# Revit family: P6 UNO XL steel base 100x100
name_source: partatom
category: Furniture
revit_build: Autodesk Revit 2017 (Build: 20160225_1515(x64)
units: mm (PartAtom-declared; Revit-internal decimal feet)

## family parameters
Always vertical = Yes
Cut with Voids When Loaded = No
OmniClass Number = 23.40.20.00
OmniClass Title = General Furniture and Specialties
Room Calculation Point = No
Shared = No
Work Plane-Based = No

## types (1)
- P6 UNO XL steel base 100x100
    Assembly Code = E2020200
    Assistance = Call for assistance number: 336.941.3446
    Collection = P6 UNO Square All Weather Umbrella
    Depth = 10 mm  [stored 0.0328084 ft]
    Description = Square umbrella XL size with Sunbrella cover and steel base 100x100
    Fabric = Color options
    Industry = Café, Restaurant, Bistro, Lounge, Hotel, Club, College
    Length = 10 mm  [stored 0.0328084 ft]
    Manufacturer = Beaufurn
    Model = P6 UNO XL steel base 100x100
    Products of collection = P6 UNO Square, P6 UNO XL Square, P6 DUO Square, P6 DUO XL Square
    Purpose = Dining, Patio/Outdoor, Pool Area
    Structure = Aluminium
    Total coverage SqFt = 100
    Type Comments = P6 Uno Square Umbrella can be used alone or combinedwith up to four other P6 Square umbrellas on a single pole
    URL = https://beaufurn.com

note: [stored X ft] marks values corroborated as IEEE doubles in the binary element streams (Revit-internal decimal feet)

## geometry (parser evidence)
native form markers: Sweep x2
no freeform markers — native parametric forms only
